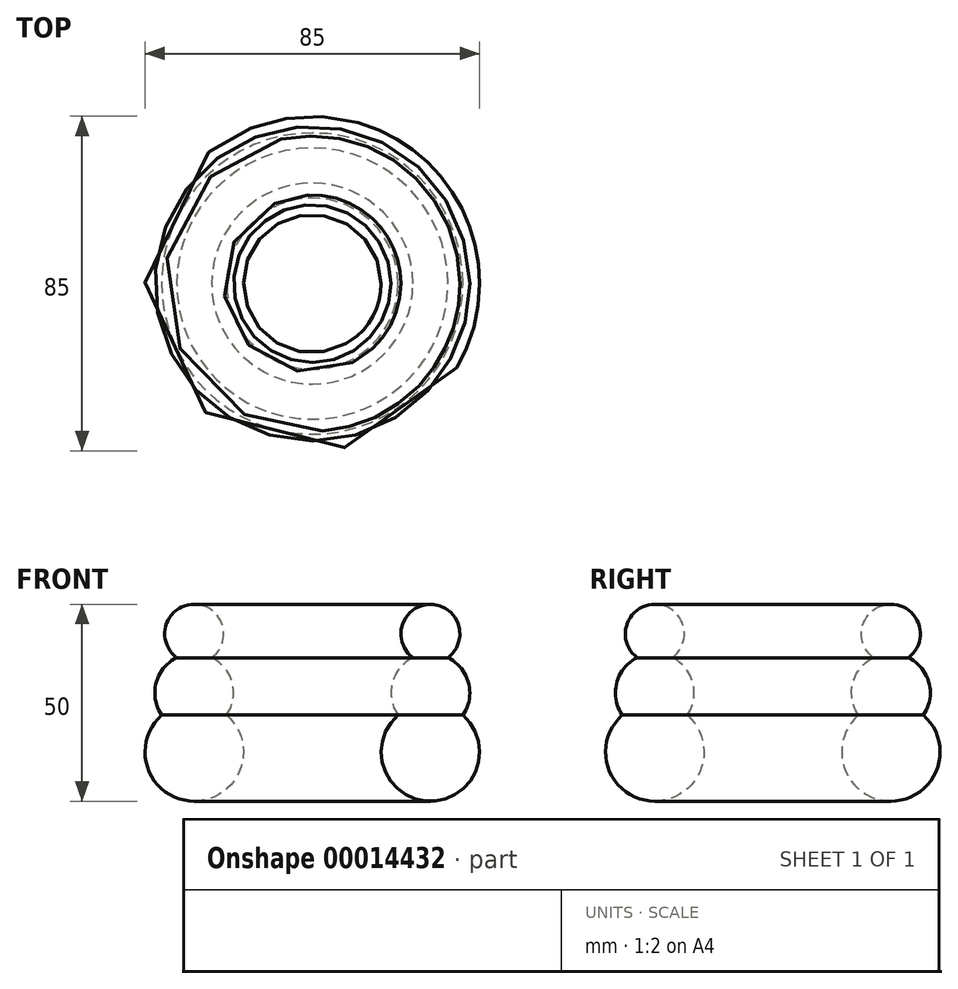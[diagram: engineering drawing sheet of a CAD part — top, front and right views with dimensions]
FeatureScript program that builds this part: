
annotation { "Feature Type Name" : "Feature", "Feature Type Description" : "" }
export const myFeature = defineFeature(function(context is Context, id is Id, definition is map)
    precondition{}
    {
        {
            var Q0;
            Q0=qCreatedBy(makeId("Front.planeOp"),FACE);
            var sketch = newSketch(context, id + "F0", { "sketchPlane" : qUnion([Q0])});
            skLineSegment(sketch, "E0", {"start": v(0, 10.77) * mm, "end": v(0, -11.77) * mm});
            skArc(sketch, "E1", {"start": v(21.73, 9.37) * mm, "mid": v(30, -12.5) * mm, "end": v(38.27, 9.38) * mm});
            skArc(sketch, "E2", {"start": v(25.56, 23.96) * mm, "mid": v(20.33, 17.54) * mm, "end": v(21.73, 9.38) * mm});
            skArc(sketch, "E3", {"start": v(34.44, 23.96) * mm, "mid": v(30, 37.5) * mm, "end": v(25.56, 23.96) * mm});
            skArc(sketch, "E4.trimOffspring", {"start": v(38.27, 9.37) * mm, "mid": v(39.67, 17.54) * mm, "end": v(34.44, 23.96) * mm});
            skSolve(sketch);
        }
        {
            var Q0;
            Q0=makeQuery(id+"F0.imprint","IMPRINT",FACE,{"disambiguationData":[TD([[makeQuery(id+"F0.imprint","IMPRINT",EDGE,{"derivedFrom":sQuery(id+"F0.wireOp",EDGE,"E1")}),1.0]])]});
            var Q1;
            Q1=sQuery(id+"F0.wireOp",EDGE,"E0");
            revolve(context, id + "F1", {"entities" : qUnion([Q0]), "axis" : qUnion([Q1]), "revolveType" : RevolveType.FULL});
        }
    });
